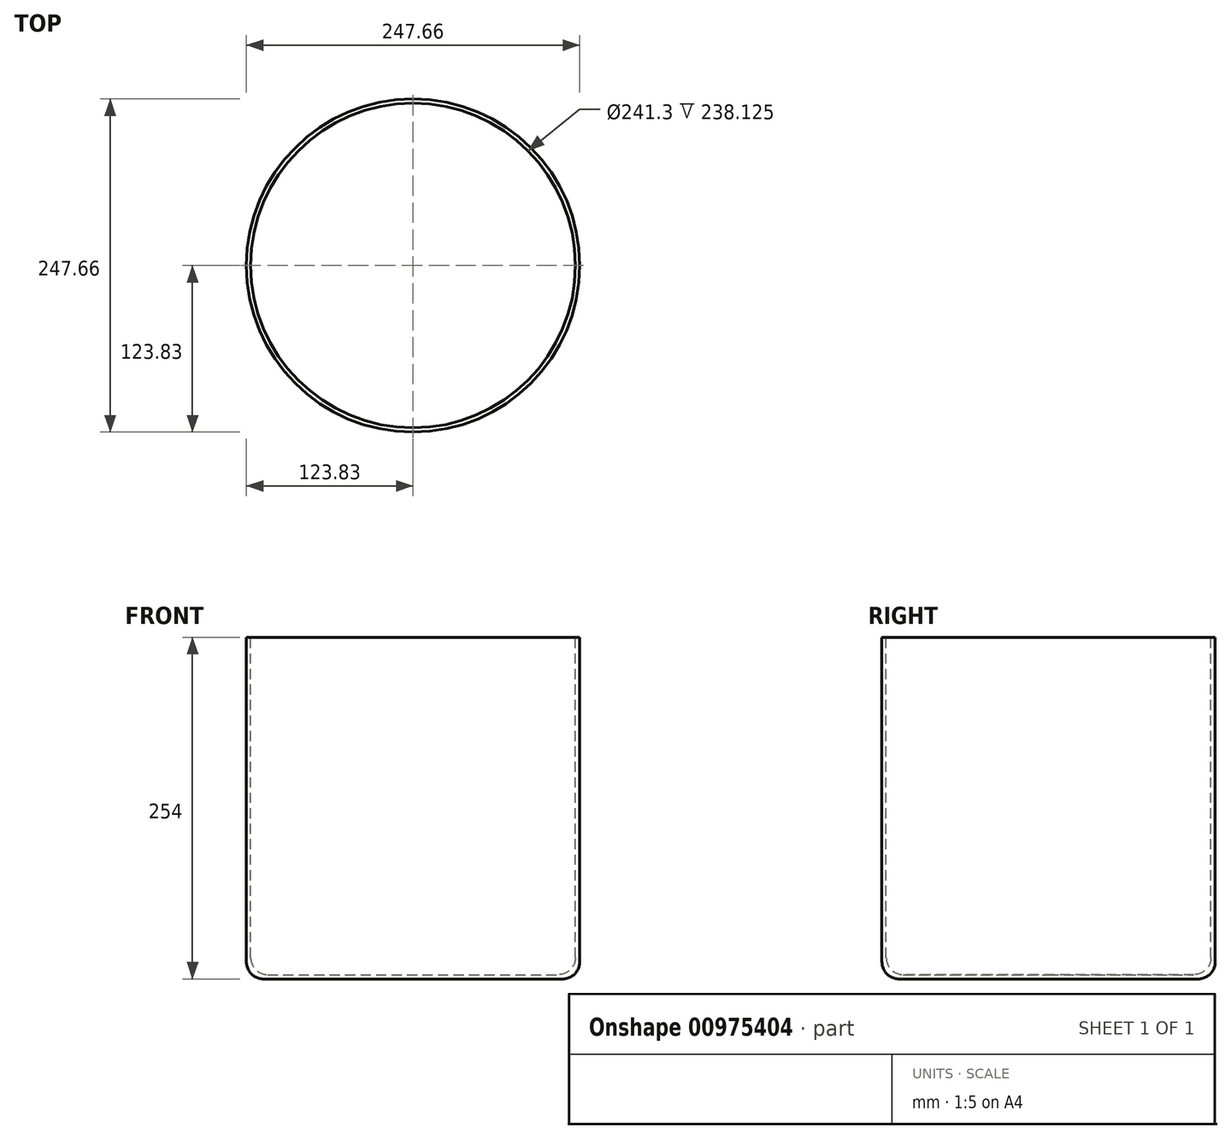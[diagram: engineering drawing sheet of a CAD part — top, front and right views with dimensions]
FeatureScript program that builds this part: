
annotation { "Feature Type Name" : "Feature", "Feature Type Description" : "" }
export const myFeature = defineFeature(function(context is Context, id is Id, definition is map)
    precondition{}
    {
        {
            var Q0;
            Q0=qCreatedBy(makeId("Top.planeOp"),FACE);
            var sketch = newSketch(context, id + "F0", { "sketchPlane" : qUnion([Q0])});
            skCircle(sketch, "E0", {"center": v(0, 0) * mm, "radius": 120.65 * mm});
            skCircle(sketch, "E1.0", {"center": v(0, 0) * mm, "radius": 123.83 * mm});
            skSolve(sketch);
        }
        {
            var Q0;
            Q0=qSketchRegion(id+"F0",true);
            extrude(context, id + "F1", {"entities" : qUnion([Q0]), "oppositeDirection" : true, "depth" : 254 * mm});
        }
        {
            var Q0;
            Q0=makeQuery(id+"F1.opExtrude","CAP_FACE",FACE,{"disambiguationData":[OSD([sQuery(id+"F0.wireOp",EDGE,"E0"),sQuery(id+"F0.wireOp",EDGE,"E1.0")])],"isStart":false});
            var sketch = newSketch(context, id + "F2", { "sketchPlane" : qUnion([Q0])});
            skCircle(sketch, "E2.0", {"center": v(0, 0) * mm, "radius": 123.83 * mm});
            skSolve(sketch);
        }
        {
            var Q0;
            Q0=qSketchRegion(id+"F2",true);
            extrude(context, id + "F3", {"entities" : qUnion([Q0]), "operationType" : NewBodyOperationType.ADD, "oppositeDirection" : true, "depth" : 3.17 * mm});
        }
        {
            var Q0;
            Q0=makeQuery(id+"F1.opExtrude","CAP_EDGE",EDGE,{"disambiguationData":[OSD([sQuery(id+"F0.wireOp",EDGE,"E1.0")])],"isStart":false});
            var Q1;
            Q1=makeQuery(id+"F3.opExtrude","CAP_FACE",FACE,{"disambiguationData":[OSD([sQuery(id+"F2.wireOp",EDGE,"E2.0")])],"isStart":false});
            fillet(context, id + "F4", {"entities" : qUnion([Q0, Q1]), "radius" : 12.7 * mm, "tangentPropagation" : true, "allowEdgeOverflow" : false});
        }
    });
